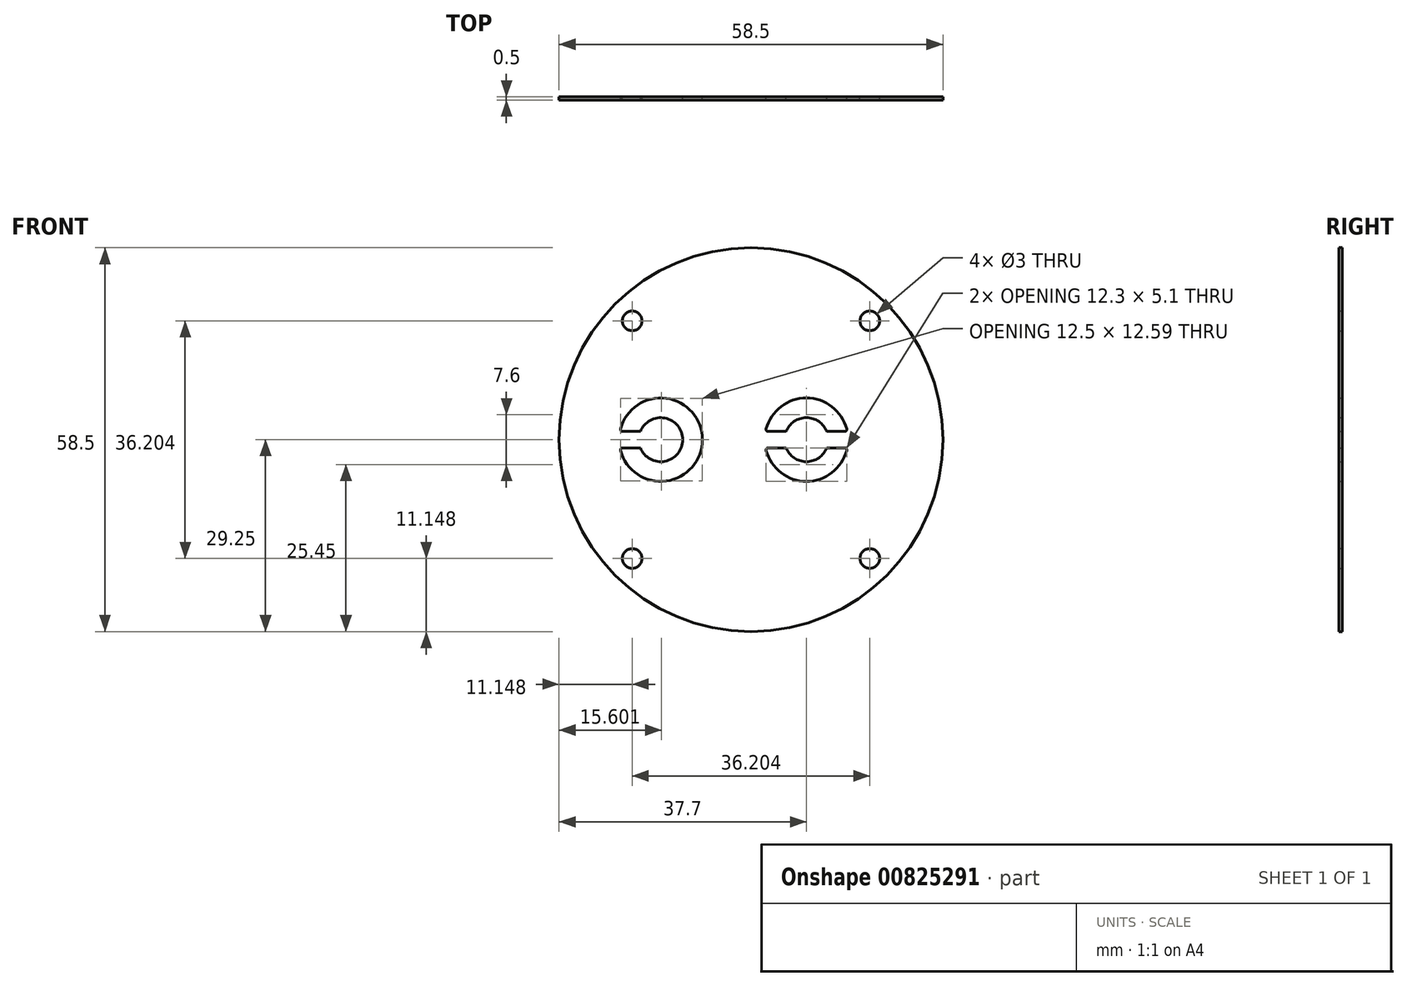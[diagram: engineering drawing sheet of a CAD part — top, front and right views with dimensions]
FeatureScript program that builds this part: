
annotation { "Feature Type Name" : "Feature", "Feature Type Description" : "" }
export const myFeature = defineFeature(function(context is Context, id is Id, definition is map)
    precondition{}
    {
        {
            var Q0;
            Q0=qCreatedBy(makeId("Front.planeOp"),FACE);
            var sketch = newSketch(context, id + "F0", { "sketchPlane" : qUnion([Q0])});
            skCircle(sketch, "E0", {"center": v(0, 0) * mm, "radius": 29.25 * mm});
            skArc(sketch, "E1", {"start": v(-19.89, -1.63) * mm, "mid": v(-7.4, 0) * mm, "end": v(-19.89, 1.63) * mm});
            skArc(sketch, "E2", {"start": v(-16.86, -1.25) * mm, "mid": v(-10.4, 0) * mm, "end": v(-16.86, 1.25) * mm});
            skLineSegment(sketch, "E3", {"start": v(-19.6, 1.25) * mm, "end": v(-16.86, 1.25) * mm});
            skLineSegment(sketch, "E4", {"start": v(-19.6, -1.25) * mm, "end": v(-16.86, -1.25) * mm});
            skLineSegment(sketch, "E5", {"start": v(0, 27.3) * mm, "end": v(0, -23.78) * mm, "construction": true});
            skPoint(sketch, "E5.endSnap0", {"position": v(0, 3.35) * mm});
            skLineSegment(sketch, "E6", {"start": v(0, 0) * mm, "end": v(-21.37, 21.37) * mm, "construction": true});
            skLineSegment(sketch, "E7", {"start": v(-34.23, 0) * mm, "end": v(2.1, 0) * mm, "construction": true});
            skCircle(sketch, "E8", {"center": v(0, 0) * mm, "radius": 25.6 * mm, "construction": true});
            skPoint(sketch, "E9", {"position": v(-18.1, 18.1) * mm});
            skPoint(sketch, "E10.1.0", {"position": v(-18.1, -18.1) * mm});
            skPoint(sketch, "E10.2.0", {"position": v(18.1, -18.1) * mm});
            skPoint(sketch, "E10.3.0", {"position": v(18.1, 18.1) * mm});
            skArc(sketch, "E11", {"start": v(2.31, -1.63) * mm, "mid": v(8.45, -6.35) * mm, "end": v(14.59, -1.63) * mm});
            skArc(sketch, "E12", {"start": v(5.34, -1.25) * mm, "mid": v(8.45, -3.35) * mm, "end": v(11.56, -1.25) * mm});
            skLineSegment(sketch, "E13", {"start": v(2.6, 1.25) * mm, "end": v(5.34, 1.25) * mm});
            skLineSegment(sketch, "E14", {"start": v(2.6, -1.25) * mm, "end": v(5.34, -1.25) * mm});
            skLineSegment(sketch, "E15.trimOffspring", {"start": v(5.1, 0) * mm, "end": v(32.63, 0) * mm, "construction": true});
            skLineSegment(sketch, "E16.trimOffspring", {"start": v(11.56, 1.25) * mm, "end": v(14.3, 1.25) * mm});
            skLineSegment(sketch, "E17.trimOffspring", {"start": v(11.56, -1.25) * mm, "end": v(14.3, -1.25) * mm});
            skArc(sketch, "E18.trimOffspring", {"start": v(11.56, 1.25) * mm, "mid": v(8.45, 3.35) * mm, "end": v(5.34, 1.25) * mm});
            skArc(sketch, "E19", {"start": v(-19.89, 1.63) * mm, "mid": v(-19.84, 1.37) * mm, "end": v(-19.6, 1.25) * mm});
            skArc(sketch, "E20", {"start": v(-19.6, -1.25) * mm, "mid": v(-19.84, -1.37) * mm, "end": v(-19.89, -1.63) * mm});
            skArc(sketch, "E21", {"start": v(2.31, 1.63) * mm, "mid": v(2.36, 1.37) * mm, "end": v(2.6, 1.25) * mm});
            skArc(sketch, "E22", {"start": v(2.6, -1.25) * mm, "mid": v(2.36, -1.37) * mm, "end": v(2.31, -1.63) * mm});
            skArc(sketch, "E23", {"start": v(14.59, -1.63) * mm, "mid": v(14.54, -1.37) * mm, "end": v(14.3, -1.25) * mm});
            skArc(sketch, "E24", {"start": v(14.3, 1.25) * mm, "mid": v(14.54, 1.37) * mm, "end": v(14.59, 1.63) * mm});
            skArc(sketch, "E25.trimOffspring", {"start": v(14.59, 1.63) * mm, "mid": v(8.45, 6.35) * mm, "end": v(2.31, 1.63) * mm});
            skSolve(sketch);
        }
        {
            var Q0;
            Q0=makeQuery(id+"F0.imprint","IMPRINT",FACE,{"disambiguationData":[TD([[makeQuery(id+"F0.imprint","IMPRINT",EDGE,{"derivedFrom":sQuery(id+"F0.wireOp",EDGE,"E0")}),1.0]])]});
            extrude(context, id + "F1", {"entities" : qUnion([Q0]), "depth" : .5 * mm, "offsetDistance" : 25 * mm});
        }
        {
            var Q0;
            Q0=sQuery(id+"F0.wireOp",VERTEX,"E9");
            var Q1;
            Q1=sQuery(id+"F0.wireOp",VERTEX,"E10.3.0");
            var Q2;
            Q2=sQuery(id+"F0.wireOp",VERTEX,"E10.2.0");
            var Q3;
            Q3=sQuery(id+"F0.wireOp",VERTEX,"E10.1.0");
            var Q4;
            Q4=makeQuery(id+"F1.opExtrude","SWEPT_BODY",BODY,{"disambiguationData":[OSD([sQuery(id+"F0.wireOp",EDGE,"E0"),sQuery(id+"F0.wireOp",EDGE,"933UWlGj-zxbM-vUyl-PWgf-o0A5Bk2zyLMK"),sQuery(id+"F0.wireOp",EDGE,"WRN3ExPu-b0c6-xeca-Ul5h-64TLUagRlNoE"),sQuery(id+"F0.wireOp",EDGE,"hPACBzxS-AL1g-GYk5-EC67-YYIK30R6SZbu"),sQuery(id+"F0.wireOp",EDGE,"2sS98eBU-3Xrg-4rCp-c2Sw-3O77hafPWSiD"),sQuery(id+"F0.wireOp",EDGE,"EUOkyvr8-5UHN-aEyS-12Pj-uURR5DR2praA"),sQuery(id+"F0.wireOp",EDGE,"RLdN2tvl-9OOy-5X6z-zZqb-VOy4vBkDxfzY"),sQuery(id+"F0.wireOp",EDGE,"866b3163-1d53-43c1-808d-e099606ec063.trimOffspring"),sQuery(id+"F0.wireOp",EDGE,"3c1e38cb-fbe2-420d-ade2-0d26bb60f305.trimOffspring"),sQuery(id+"F0.wireOp",EDGE,"E1"),sQuery(id+"F0.wireOp",EDGE,"E2"),sQuery(id+"F0.wireOp",EDGE,"E3"),sQuery(id+"F0.wireOp",EDGE,"E4")])]});
            hole(context, id + "F2", {"style" : HoleStyle.SIMPLE, "endStyle" : HoleEndStyle.THROUGH, "oppositeDirection" : true, "holeDiameter" : 3 * mm, "majorDiameter" : 5 * mm, "isTappedThrough" : true, "tappedDepth" : 12 * mm, "tapClearance" : 3, "locations" : qUnion([Q0, Q1, Q2, Q3]), "scope" : qUnion([Q4])});
        }
    });
